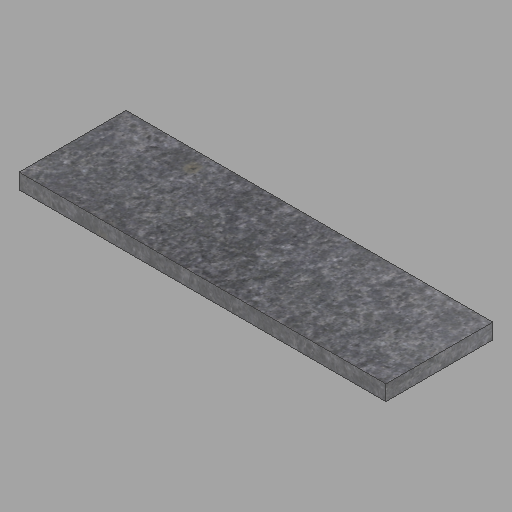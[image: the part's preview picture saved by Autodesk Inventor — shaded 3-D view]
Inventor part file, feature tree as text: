
AUTODESK INVENTOR PART (.ipt)
format: ipt  version: 2023 (Build 270158000, 158)  size: 203,264 bytes
history: native  units: in
note: dims shown in document units (in); Inventor stores cm internally (conversion verified against a paired STEP export)
features: other x1, extrude x1, sketch x1
ambient origin geometry x8: Origin, YZ Plane, XZ Plane, XY Plane, X Axis, Y Axis, Z Axis, Center Point
bodies: Solid1 (feature_tree)
feature tree (3):
  other  "2x14x48-3"
  extrude  "Extrusion1"  Depth=14.0in
  sketch  "Sketch1"  dims[d0=2.0in d1=14.0in d2=48.0in d3=0.0in]
